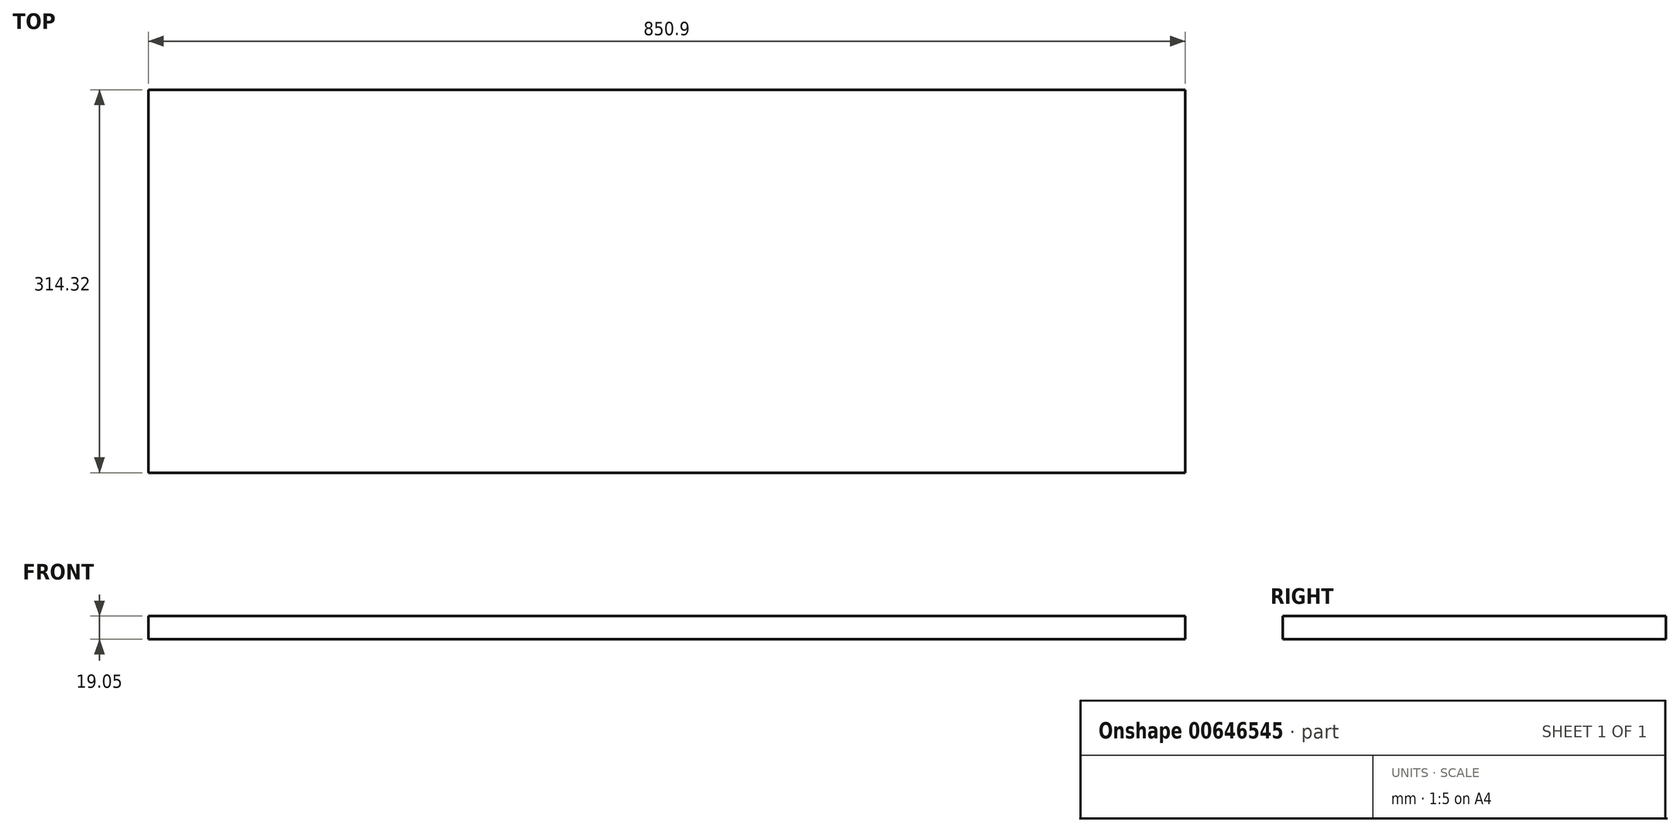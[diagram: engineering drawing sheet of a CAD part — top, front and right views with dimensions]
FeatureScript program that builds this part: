
annotation { "Feature Type Name" : "Feature", "Feature Type Description" : "" }
export const myFeature = defineFeature(function(context is Context, id is Id, definition is map)
    precondition{}
    {
        {
            var Q0;
            Q0=qCreatedBy(makeId("Top.planeOp"),FACE);
            var sketch = newSketch(context, id + "F0", { "sketchPlane" : qUnion([Q0])});
            skLineSegment(sketch, "E0.bottom", {"start": v(425.45, 157.16) * mm, "end": v(-425.45, 157.16) * mm});
            skLineSegment(sketch, "E0.top", {"start": v(425.45, -157.16) * mm, "end": v(-425.45, -157.16) * mm});
            skLineSegment(sketch, "E0.left", {"start": v(425.45, 157.16) * mm, "end": v(425.45, -157.16) * mm});
            skLineSegment(sketch, "E0.right", {"start": v(-425.45, 157.16) * mm, "end": v(-425.45, -157.16) * mm});
            skPoint(sketch, "E0.middle", {"position": v(0, 0) * mm});
            skSolve(sketch);
        }
        {
            var Q0;
            Q0=makeQuery(id+"F0.imprint","IMPRINT",FACE,{"disambiguationData":[TD([[makeQuery(id+"F0.imprint","IMPRINT",EDGE,{"derivedFrom":sQuery(id+"F0.wireOp",EDGE,"E0.bottom")}),1.0]])]});
            extrude(context, id + "F1", {"entities" : qUnion([Q0]), "depth" : 19.05 * mm, "offsetDistance" : 25.4 * mm});
        }
    });
